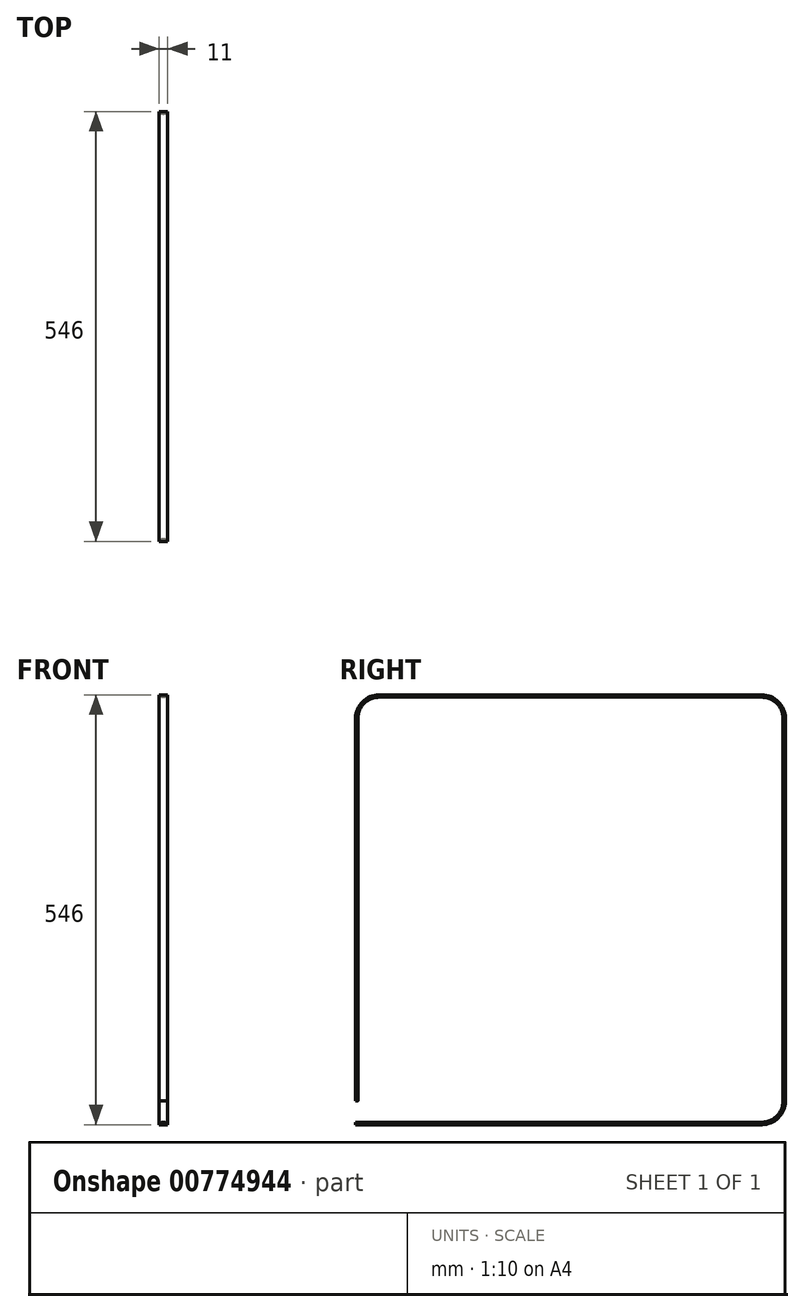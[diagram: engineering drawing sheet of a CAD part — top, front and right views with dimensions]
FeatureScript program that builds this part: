
annotation { "Feature Type Name" : "Feature", "Feature Type Description" : "" }
export const myFeature = defineFeature(function(context is Context, id is Id, definition is map)
    precondition{}
    {
        {
            var Q0;
            Q0=qCreatedBy(makeId("Front.planeOp"),FACE);
            var sketch = newSketch(context, id + "F0", { "sketchPlane" : qUnion([Q0])});
            skLineSegment(sketch, "E0.bottom", {"start": v(-5.5, 0) * mm, "end": v(5.5, 0) * mm, "construction": true});
            skLineSegment(sketch, "E0.top", {"start": v(-5.5, 3) * mm, "end": v(5.5, 3) * mm, "construction": true});
            skLineSegment(sketch, "E0.left", {"start": v(-5.5, 0) * mm, "end": v(-5.5, 3) * mm, "construction": true});
            skLineSegment(sketch, "E0.right", {"start": v(5.5, 0) * mm, "end": v(5.5, 3) * mm, "construction": true});
            skLineSegment(sketch, "E1", {"start": v(0, 0) * mm, "end": v(0, 14.13) * mm, "construction": true});
            skLineSegment(sketch, "E2", {"start": v(-5.5, 0) * mm, "end": v(5.5, 0) * mm});
            skArc(sketch, "E3", {"start": v(5.5, 0) * mm, "mid": v(0, 3) * mm, "end": v(-5.5, 0) * mm});
            skSolve(sketch);
        }
        {
            var Q0;
            Q0=qCreatedBy(makeId("Right.planeOp"),FACE);
            var sketch = newSketch(context, id + "F1", { "sketchPlane" : qUnion([Q0])});
            skLineSegment(sketch, "E4", {"start": v(0, 0) * mm, "end": v(516, 0) * mm});
            skLineSegment(sketch, "E5", {"start": v(546, 30) * mm, "end": v(546, 516) * mm});
            skLineSegment(sketch, "E6", {"start": v(516, 546) * mm, "end": v(30, 546) * mm});
            skLineSegment(sketch, "E7", {"start": v(0, 546) * mm, "end": v(0, 546) * mm});
            skLineSegment(sketch, "E8", {"start": v(0, 30.16) * mm, "end": v(0, 516) * mm});
            skPoint(sketch, "E9.visualSharp", {"position": v(546, 0) * mm});
            skArc(sketch, "E9.filletArc", {"start": v(516, 0) * mm, "mid": v(537.21, 8.79) * mm, "end": v(546, 30) * mm});
            skPoint(sketch, "E10.visualSharp", {"position": v(546, 546) * mm});
            skArc(sketch, "E10.filletArc", {"start": v(546, 516) * mm, "mid": v(537.21, 537.21) * mm, "end": v(516, 546) * mm});
            skPoint(sketch, "E11.visualSharp", {"position": v(0, 546) * mm});
            skArc(sketch, "E11.filletArc", {"start": v(30, 546) * mm, "mid": v(8.79, 537.21) * mm, "end": v(0, 516) * mm});
            skSolve(sketch);
        }
        {
            var Q0;
            Q0=makeQuery(id+"F0.imprint","IMPRINT",FACE,{"disambiguationData":[TD([[makeQuery(id+"F0.imprint","IMPRINT",EDGE,{"derivedFrom":sQuery(id+"F0.wireOp",EDGE,"E2")}),1.0]])]});
            var Q1;
            Q1=sQuery(id+"F1.wireOp",EDGE,"E4");
            var Q2;
            Q2=sQuery(id+"F1.wireOp",EDGE,"E9.filletArc");
            var Q3;
            Q3=sQuery(id+"F1.wireOp",EDGE,"E5");
            var Q4;
            Q4=sQuery(id+"F1.wireOp",EDGE,"E10.filletArc");
            var Q5;
            Q5=sQuery(id+"F1.wireOp",EDGE,"E6");
            var Q6;
            Q6=sQuery(id+"F1.wireOp",EDGE,"E11.filletArc");
            var Q7;
            Q7=sQuery(id+"F1.wireOp",EDGE,"E8");
            sweep(context, id + "F2", {"profiles" : qUnion([Q0]), "path" : qUnion([Q1, Q2, Q3, Q4, Q5, Q6, Q7])});
        }
    });
